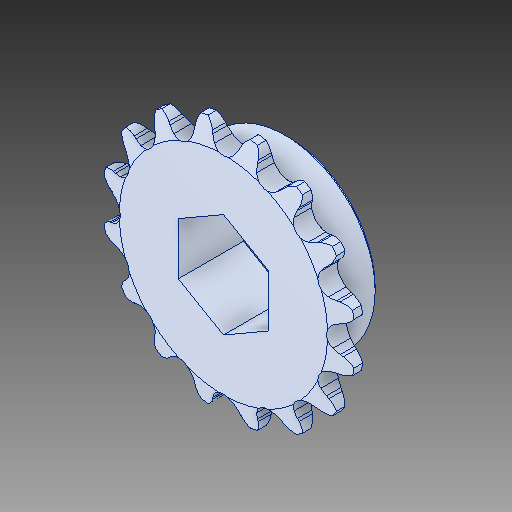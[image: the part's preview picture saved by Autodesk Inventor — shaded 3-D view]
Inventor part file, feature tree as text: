
AUTODESK INVENTOR PART (.ipt)
format: ipt  version: 2018 (Build 220112000, 112)  size: 478,720 bytes
history: native  units: in
note: dims shown in document units (in); Inventor stores cm internally (conversion verified against a paired STEP export)
features: chamfer x1
ambient origin geometry x8: Origin, YZ Plane, XZ Plane, XY Plane, X Axis, Y Axis, Z Axis, Center Point
bodies: Solid1 (feature_tree)
feature tree (1):
  chamfer  "Chamfer2"  [1 undecoded]
note: 1 required parameter value undecoded (feature->parameter linkage not recoverable at this tier; creation-order binding heuristic only, values carry confidence <= 0.55)
